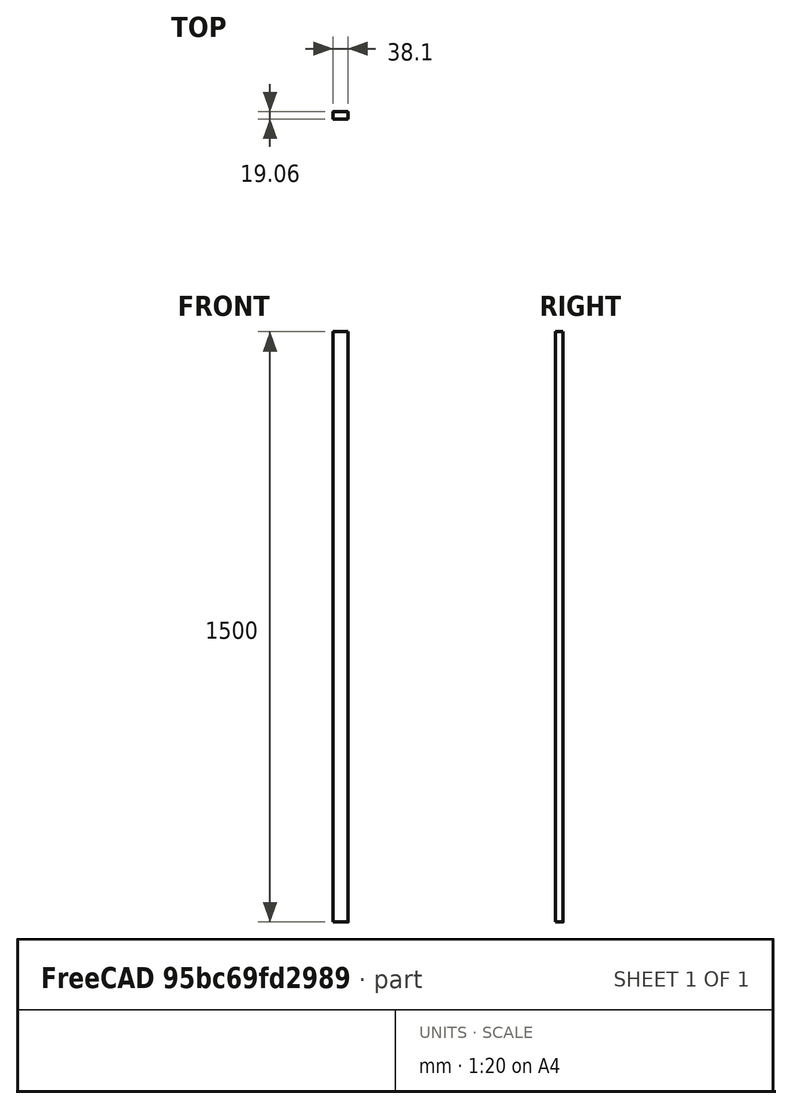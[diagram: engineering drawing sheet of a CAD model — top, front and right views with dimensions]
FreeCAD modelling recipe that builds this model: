
FCSTD DOCUMENT  (FreeCAD 0.20R29177 +426 (Git))
Label: Arm
License: All rights reserved
LicenseURL: http://en.wikipedia.org/wiki/All_rights_reserved
objects: PartDesign::CoordinateSystem×3, Sketcher::SketchObject×1, App::FeaturePython×1, PartDesign::Pad×1, PartDesign::Body×1, App::Part×1
note: 7 computed .brp shape members not serialized (recipe doc carries the construction recipe); baked Part::Feature solids carry a one-line shape summary decoded from their .brp

FEATURE [Sketcher::SketchObject] Sketch
  FullyConstrained = true
  MapMode = 5
  Support = -> [XY_Plane001]
  expr: Constraints[16] = <<Variables>>.FilletRadius
  expr: Constraints[18] = <<Variables>>.Dim1
  expr: Constraints[19] = <<Variables>>.Dim2
  sketch-geometry (9):
    g0: LineSegment StartX=-19.05 StartY=9.025 StartZ=0 EndX=-19.05 EndY=-9.025 EndZ=0
    g1: LineSegment StartX=-18.55 StartY=-9.525 StartZ=0 EndX=18.55 EndY=-9.525 EndZ=0
    g2: LineSegment StartX=19.05 StartY=-9.025 StartZ=0 EndX=19.05 EndY=9.025 EndZ=0
    g3: LineSegment StartX=18.55 StartY=9.525 StartZ=0 EndX=-18.55 EndY=9.525 EndZ=0
    g4: GeomPoint X=0 Y=0 Z=0
    g5: ArcOfCircle CenterX=-18.55 CenterY=9.025 CenterZ=0 NormalX=0 NormalY=0 NormalZ=1 AngleXU=0 Radius=0.5 StartAngle=1.5708 EndAngle=3.14159
    g6: ArcOfCircle CenterX=-18.55 CenterY=-9.025 CenterZ=0 NormalX=0 NormalY=0 NormalZ=1 AngleXU=0 Radius=0.5 StartAngle=3.14159 EndAngle=4.71239
    g7: ArcOfCircle CenterX=18.55 CenterY=9.025 CenterZ=0 NormalX=0 NormalY=0 NormalZ=1 AngleXU=0 Radius=0.5 StartAngle=1.95e-14 EndAngle=1.5708
    g8: ArcOfCircle CenterX=18.55 CenterY=-9.025 CenterZ=0 NormalX=0 NormalY=0 NormalZ=1 AngleXU=0 Radius=0.5 StartAngle=4.71239 EndAngle=6.28319
  constraints (20):
    c: Horizontal(g1)
    c: Horizontal(g3)
    c: Vertical(g0)
    c: Vertical(g2)
    c: Coincident(g4,g-1)
    c: Tangent(g3,g5) = -1.5708
    c: Tangent(g0,g5) = -1.5708
    c: Tangent(g0,g6) = -1.5708
    c: Tangent(g1,g6) = -1.5708
    c: Tangent(g3,g7) = -1.5708
    c: Tangent(g2,g7) = -1.5708
    c: Tangent(g2,g8) = -1.5708
    c: Tangent(g1,g8) = -1.5708
    c: Equal(g8,g7)
    c: Equal(g7,g5)
    c: Equal(g5,g6)
    c: Radius(g7) = 0.5
    c: Symmetric(g7,g6,g4)
    c: DistanceY(g1,g3) = 19.05
    c: DistanceX(g0,g2) = 38.1
FEATURE [App::FeaturePython] Variables  # WARN: FeaturePython — macro-defined, semantics opaque (R4)
  Dim1 = 19.05
  Dim2 = 38.1
  FilletRadius = 0.5
  Length = 1500
  Type = App::PropertyContainer
FEATURE [PartDesign::Pad] Pad
  Direction = (0,0,1)
  Length = 1500
  Length2 = 10
  Midplane = true
  Profile = -> Sketch
  ReferenceAxis = -> Sketch [N_Axis]
  Type = 0
  expr: Length = <<Variables>>.Length
FEATURE [PartDesign::Body] Body
  Group = -> [Sketch,Pad]
  Origin = -> Origin001
  Tip = -> Pad
FEATURE [PartDesign::CoordinateSystem] LCS_Center
  AttacherType = Attacher::AttachEngine3D
  MapMode = 2
  Support = -> [XY_Plane]
FEATURE [PartDesign::CoordinateSystem] LCS_End1
  AttacherType = Attacher::AttachEngine3D
  AttachmentOffset = pos=(0,0,750) rot=(0,0,1;0rad)
  MapMode = 2
  Placement = pos=(0,0,750) rot=(0,0,1;0rad)
  Support = -> [XY_Plane]
  expr: .AttachmentOffset.Base.z = <<Variables>>.Length / 2
FEATURE [PartDesign::CoordinateSystem] LCS_End2
  AttacherType = Attacher::AttachEngine3D
  AttachmentOffset = pos=(0,0,-750) rot=(0,0,1;0rad)
  MapMode = 2
  Placement = pos=(0,0,-750) rot=(0,0,1;0rad)
  Support = -> [XY_Plane]
  expr: .AttachmentOffset.Base.z = <<Variables>>.Length / -2
FEATURE [App::Part] Part
  Group = -> [Body,Variables,LCS_Center,LCS_End1,LCS_End2]
  Origin = -> Origin
  Type = Asm4::VariantLink
